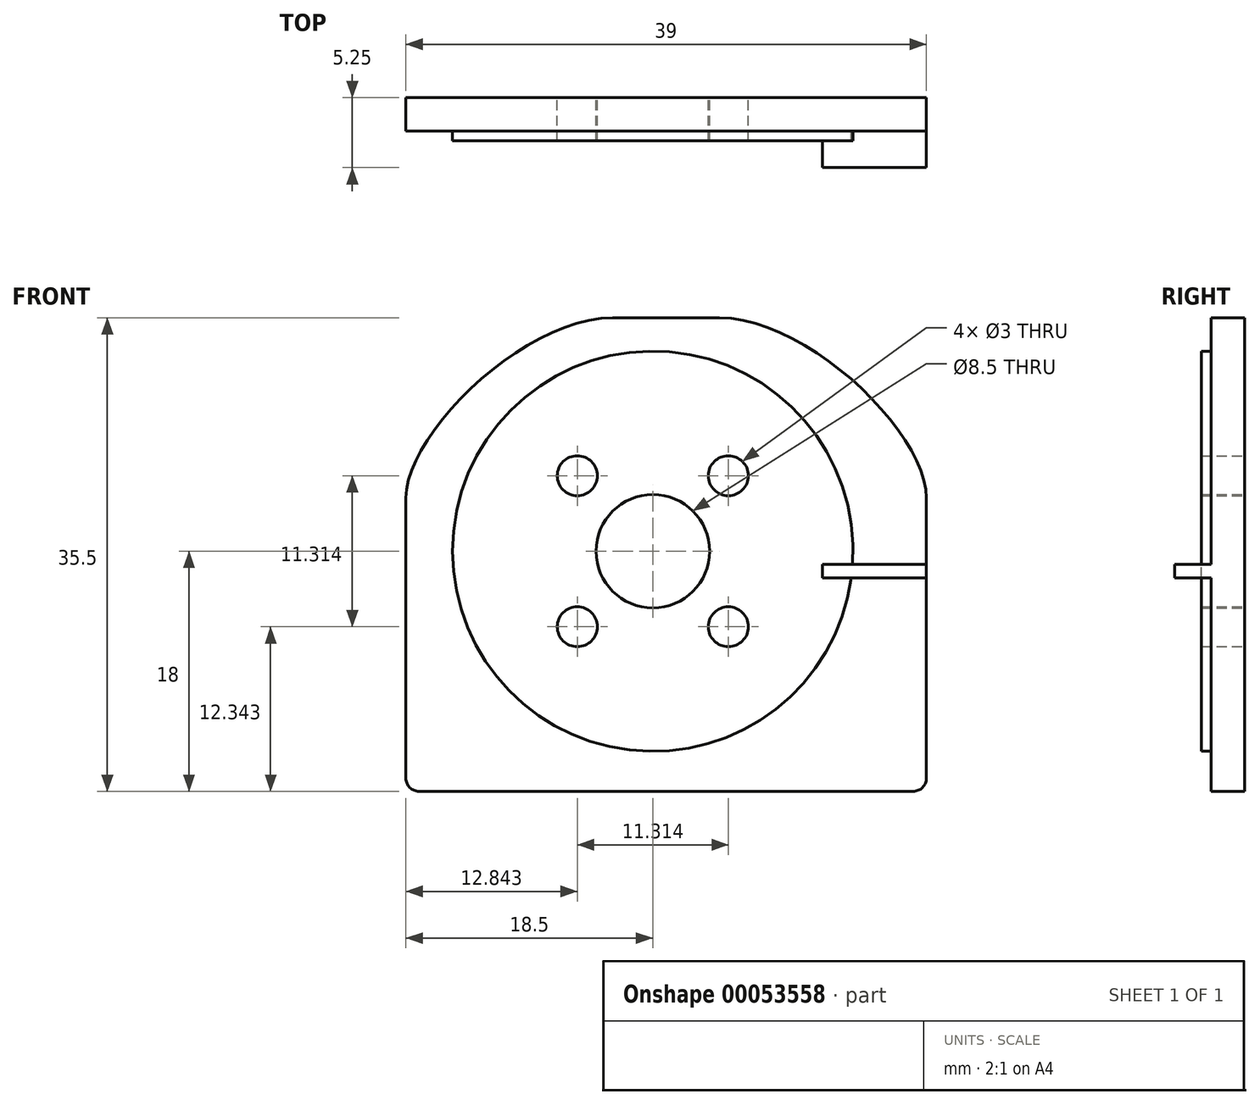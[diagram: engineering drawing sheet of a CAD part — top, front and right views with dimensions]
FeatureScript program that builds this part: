
annotation { "Feature Type Name" : "Feature", "Feature Type Description" : "" }
export const myFeature = defineFeature(function(context is Context, id is Id, definition is map)
    precondition{}
    {
        {
            var Q0;
            Q0=qCreatedBy(makeId("Front.planeOp"),FACE);
            var sketch = newSketch(context, id + "F0", { "sketchPlane" : qUnion([Q0])});
            skLineSegment(sketch, "E0.bottom", {"start": v(19.5, -17.75) * mm, "end": v(-19.5, -17.75) * mm, "construction": true});
            skLineSegment(sketch, "E0.top", {"start": v(19.5, 17.75) * mm, "end": v(-19.5, 17.75) * mm, "construction": true});
            skLineSegment(sketch, "E0.left", {"start": v(19.5, -17.75) * mm, "end": v(19.5, 17.75) * mm, "construction": true});
            skLineSegment(sketch, "E0.right", {"start": v(-19.5, -17.75) * mm, "end": v(-19.5, 17.75) * mm, "construction": true});
            skPoint(sketch, "E0.middle", {"position": v(0, 0) * mm});
            skLineSegment(sketch, "E1", {"start": v(0, 17.75) * mm, "end": v(4, 17.75) * mm});
            skLineSegment(sketch, "E2.MirrorCS", {"start": v(0, 17.75) * mm, "end": v(-4, 17.75) * mm});
            skLineSegment(sketch, "E3", {"start": v(-19.5, 4.25) * mm, "end": v(19.5, 4.25) * mm, "construction": true});
            skLineSegment(sketch, "E4", {"start": v(-19.5, 4.25) * mm, "end": v(-19.5, -17.75) * mm});
            skLineSegment(sketch, "E5", {"start": v(19.5, -17.75) * mm, "end": v(19.5, 4.25) * mm});
            skFitSpline(sketch, "E6", {"points": [v(4, 17.75) * mm, v(19.5, 4.25) * mm], "startDerivative": vector(20, 0) * mm, "endDerivative": vector(0, -14.42) * mm});
            skFitSpline(sketch, "E7.MirrorCS", {"points": [v(-4, 17.75) * mm, v(-19.5, 4.25) * mm], "startDerivative": vector(-20, 0) * mm, "endDerivative": vector(0, -14.42) * mm});
            skLineSegment(sketch, "E8", {"start": v(-19.5, -17.75) * mm, "end": v(19.5, -17.75) * mm});
            skCircle(sketch, "E9", {"center": v(-1, 0.25) * mm, "radius": 4.25 * mm});
            skCircle(sketch, "E10", {"center": v(-1, 0.25) * mm, "radius": 8 * mm, "construction": true});
            skLineSegment(sketch, "E11", {"start": v(-1, 0.25) * mm, "end": v(4.66, 5.9) * mm, "construction": true});
            skLineSegment(sketch, "E12", {"start": v(-1, 0.25) * mm, "end": v(7, 0.25) * mm, "construction": true});
            skCircle(sketch, "E13", {"center": v(4.66, 5.9) * mm, "radius": 1.5 * mm});
            skCircle(sketch, "E14.1.0", {"center": v(-6.66, 5.9) * mm, "radius": 1.5 * mm});
            skCircle(sketch, "E14.2.0", {"center": v(-6.66, -5.4) * mm, "radius": 1.5 * mm});
            skCircle(sketch, "E14.3.0", {"center": v(4.66, -5.4) * mm, "radius": 1.5 * mm});
            skCircle(sketch, "E15", {"center": v(-1, 0.25) * mm, "radius": 15 * mm, "construction": true});
            skSolve(sketch);
        }
        {
            var Q0;
            Q0 = qSketchRegion(id + "F0", true);
            extrude(context, id + "F1", {"entities" : qUnion([Q0]), "depth" : 2.5 * mm, "symmetric" : true});
        }
        {
            var Q0;
            Q0=qCreatedBy(makeId("Front.planeOp"),FACE);
            var sketch = newSketch(context, id + "F2", { "sketchPlane" : qUnion([Q0])});
            skCircle(sketch, "E16.0", {"center": v(-6.66, 5.9) * mm, "radius": 1.5 * mm});
            skCircle(sketch, "E16.1", {"center": v(4.66, 5.9) * mm, "radius": 1.5 * mm});
            skCircle(sketch, "E16.2", {"center": v(4.66, -5.4) * mm, "radius": 1.5 * mm});
            skCircle(sketch, "E16.3", {"center": v(-6.66, -5.4) * mm, "radius": 1.5 * mm});
            skCircle(sketch, "E16.4", {"center": v(-1, 0.25) * mm, "radius": 4.25 * mm});
            skCircle(sketch, "E17", {"center": v(-1, 0.25) * mm, "radius": 15 * mm});
            skSolve(sketch);
        }
        {
            var Q0;
            Q0 = qSketchRegion(id + "F2", true);
            extrude(context, id + "F3", {"entities" : qUnion([Q0]), "operationType" : NewBodyOperationType.ADD, "depth" : 2 * mm});
        }
        {
            var Q0;
            Q0=makeQuery(id+"F3.opExtrude","CAP_FACE",FACE,{"disambiguationData":[OSD([sQuery(id+"F2.wireOp",EDGE,"E16.0"),sQuery(id+"F2.wireOp",EDGE,"E16.1"),sQuery(id+"F2.wireOp",EDGE,"E16.2"),sQuery(id+"F2.wireOp",EDGE,"E16.3"),sQuery(id+"F2.wireOp",EDGE,"E16.4"),sQuery(id+"F2.wireOp",EDGE,"E17")])],"isStart":false});
            var sketch = newSketch(context, id + "F4", { "sketchPlane" : qUnion([Q0])});
            skLineSegment(sketch, "E18.0", {"start": v(-19.5, -17.75) * mm, "end": v(19.5, -17.75) * mm, "construction": true});
            skLineSegment(sketch, "E19", {"start": v(-23.42, -1.25) * mm, "end": v(26.23, -1.25) * mm, "construction": true});
            skLineSegment(sketch, "E20.0", {"start": v(19.5, -17.75) * mm, "end": v(19.5, 4.25) * mm, "construction": true});
            skLineSegment(sketch, "E21", {"start": v(19.5, -1.25) * mm, "end": v(19.5, -0.75) * mm});
            skLineSegment(sketch, "E22", {"start": v(19.5, -0.75) * mm, "end": v(11.7, -0.75) * mm});
            skLineSegment(sketch, "E23", {"start": v(11.7, -0.75) * mm, "end": v(11.7, -1.25) * mm});
            skLineSegment(sketch, "E24.MirrorCS", {"start": v(11.7, -1.75) * mm, "end": v(11.7, -1.25) * mm});
            skLineSegment(sketch, "E25.MirrorCS", {"start": v(19.5, -1.75) * mm, "end": v(11.7, -1.75) * mm});
            skLineSegment(sketch, "E26.MirrorCS", {"start": v(19.5, -1.25) * mm, "end": v(19.5, -1.75) * mm});
            skSolve(sketch);
        }
        {
            var Q0;
            Q0 = qSketchRegion(id + "F4", true);
            var Q1;
            Q1=makeQuery(id+"F1.opExtrude","CAP_FACE",FACE,{"disambiguationData":[OSD([sQuery(id+"F0.wireOp",EDGE,"E1"),sQuery(id+"F0.wireOp",EDGE,"E2.MirrorCS"),sQuery(id+"F0.wireOp",EDGE,"E4"),sQuery(id+"F0.wireOp",EDGE,"E5"),sQuery(id+"F0.wireOp",EDGE,"E6"),sQuery(id+"F0.wireOp",EDGE,"E7.MirrorCS"),sQuery(id+"F0.wireOp",EDGE,"E8"),sQuery(id+"F0.wireOp",EDGE,"E9"),sQuery(id+"F0.wireOp",EDGE,"E13"),sQuery(id+"F0.wireOp",EDGE,"E14.1.0"),sQuery(id+"F0.wireOp",EDGE,"E14.2.0"),sQuery(id+"F0.wireOp",EDGE,"E14.3.0")])],"isStart":false});
            extrude(context, id + "F5", {"entities" : qUnion([Q0]), "operationType" : NewBodyOperationType.ADD, "depth" : 2 * mm, "hasSecondDirection" : true, "secondDirectionBound" : BoundingType.UP_TO_SURFACE, "secondDirectionOppositeDirection" : true, "secondDirectionBoundEntityFace" : qUnion([Q1]), "secondDirectionDepth" : 25 * mm});
        }
        {
            var Q0;
            Q0=makeQuery(id+"F1.opExtrude","SWEPT_EDGE",EDGE,{"disambiguationData":[OSD([sQuery(id+"F0.wireOp",EDGE,"E5"),sQuery(id+"F0.wireOp",EDGE,"E8")])]});
            var Q1;
            Q1=makeQuery(id+"F1.opExtrude","SWEPT_EDGE",EDGE,{"disambiguationData":[OSD([sQuery(id+"F0.wireOp",EDGE,"E4"),sQuery(id+"F0.wireOp",EDGE,"E8")])]});
            fillet(context, id + "F6", {"entities" : qUnion([Q0, Q1]), "radius" : 1 * mm, "tangentPropagation" : true, "allowEdgeOverflow" : false});
        }
    });
